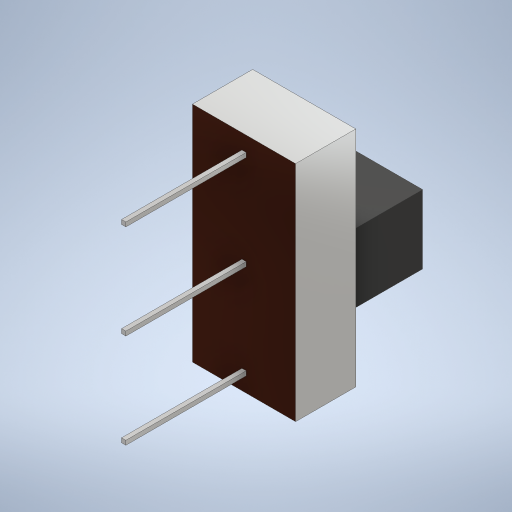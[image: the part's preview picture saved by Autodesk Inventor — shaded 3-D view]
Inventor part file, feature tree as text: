
AUTODESK INVENTOR PART (.ipt)
format: ipt  version: 2023 (Build 270158000, 158)  size: 293,888 bytes
history: native  units: mm
features: extrude x4, sketch x4
ambient origin geometry x8: Origin, YZ Plane, XZ Plane, XY Plane, X Axis, Y Axis, Z Axis, Center Point
bodies: Solid1 (feature_tree)
feature tree (8):
  extrude  "Extrusion1"  Depth=13.0mm
  extrude  "Extrusion3"  Depth=3.0mm
  extrude  "Extrusion4"  Depth=4.0mm
  extrude  "Extrusion5"  Depth=5.0mm TaperAngle=0.0deg
  sketch  "Sketch1"  dims[d0=6.0mm d1=13.0mm]
  sketch  "Sketch2"  dims[d2=3.5mm d3=0.0mm d5=3.0mm]
  sketch  "Sketch3"  dims[d18=0.11mm d19=0.0mm d20=4.0mm]
  sketch  "Sketch4"  dims[d21=4.0mm d22=5.0mm d23=0.0mm d24=1.0mm d25=90.0deg d26=0.25mm d27=0.25mm d28=1.0mm d29=90.0deg d30=0.25mm d31=0.25mm d33=90.0deg d34=0.25mm d35=0.25mm d36=7.0mm d37=0.0mm d39=5.5mm d40=5.5mm d41=3.0mm d42=1.0mm d44=1.0mm d45=3.0mm]
